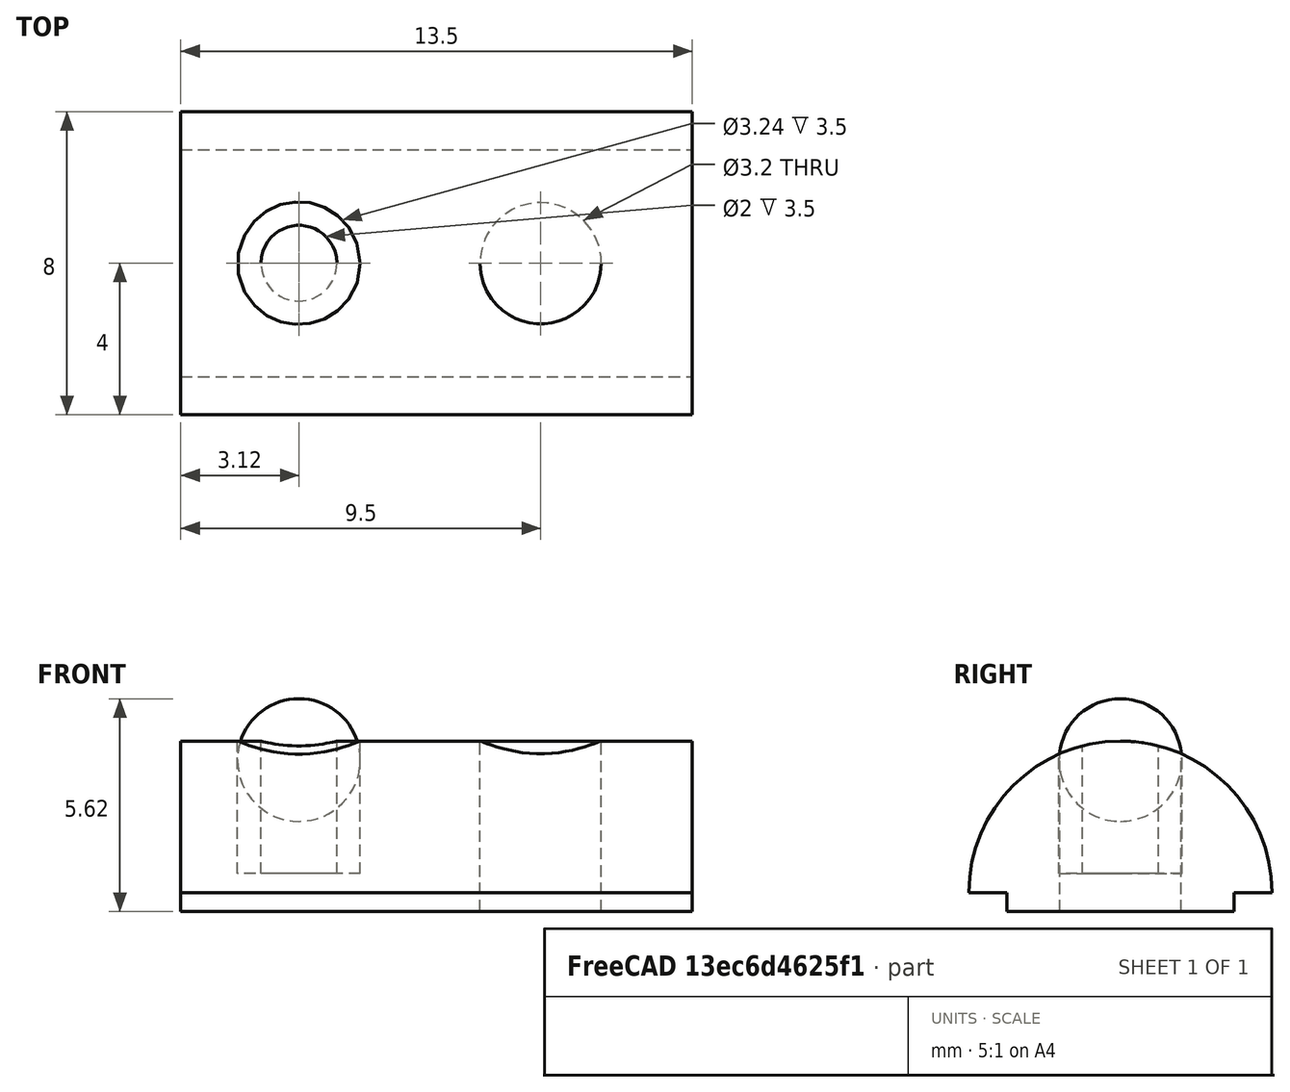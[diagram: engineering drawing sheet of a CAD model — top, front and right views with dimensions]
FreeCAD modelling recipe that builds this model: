
FCSTD DOCUMENT  (FreeCAD 0.17R13050 (Git))
Label: T-slot_2020_round_roll-in_nut_M4
License: All rights reserved
LicenseURL: http://en.wikipedia.org/wiki/All_rights_reserved
objects: Part::Cylinder×3, Part::Cut×2, Part::Sphere×1, Part::Box×1, Part::MultiFuse×1, Part::Feature×1, App::Part×1
note: 9 computed .brp shape members not serialized (recipe doc carries the construction recipe); baked Part::Feature solids carry a one-line shape summary decoded from their .brp

FEATURE [Part::Cylinder] Cylinder002
  Angle = 360
  AttacherType = Attacher::AttachEngine3D
  Height = 4.5
  Placement = pos=(9.5,3,0) rot=(0,0,1;0rad)
  Radius = 1.6
FEATURE [Part::Sphere] Sphere
  Angle1 = -90
  Angle2 = 90
  Angle3 = 360
  AttacherType = Attacher::AttachEngine3D
  Placement = pos=(3.12,3,4) rot=(0,1,0;1.5708rad)
  Radius = 1.62
FEATURE [Part::Cylinder] Cylinder001
  Angle = 360
  AttacherType = Attacher::AttachEngine3D
  Height = 3.5
  Placement = pos=(3.12,3,1) rot=(0,0,1;0rad)
  Radius = 1
FEATURE [Part::Cylinder] Cylinder
  Angle = 180
  AttacherType = Attacher::AttachEngine3D
  Height = 13.5
  Placement = pos=(0,3,0.5) rot=(0.57735,0.57735,0.57735;2.0944rad)
  Radius = 4
FEATURE [Part::Box] Box  label="Cube"
  AttacherType = Attacher::AttachEngine3D
  Height = 0.5
  Length = 13.5
  Width = 6
FEATURE [Part::MultiFuse] Fusion
  Shapes = -> [Cylinder,Box]
FEATURE [Part::Cut] Cut  label="src"
  Base = -> Fusion
  Tool = -> Cylinder001
FEATURE [Part::Feature] Cut001
  shape: bbox 13.5 x 8 x 4.5 mm, 10 faces (baked)
FEATURE [Part::Cut] Cut002
  Base = -> Cut001
  Tool = -> Cylinder002
FEATURE [App::Part] Part  label="T-slot_2020_round_roll-in_nut_M4"
  Group = -> [Sphere,Cylinder001,Cylinder,Fusion,Box,Cut,Cut001,Cylinder002,Cut002]
  License = CC BY 3.0
  LicenseURL = http://creativecommons.org/licenses/by/3.0/
  Origin = -> Origin
